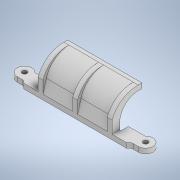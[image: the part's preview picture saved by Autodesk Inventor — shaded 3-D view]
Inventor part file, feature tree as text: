
AUTODESK INVENTOR PART (.ipt)
format: ipt  version: 2022 (Build 260153000, 153)  size: 208,384 bytes
history: native  units: mm
features: sketch x4, extrude x3, mirror x1, plane x1, pattern_linear x1
ambient origin geometry x8: Origin, YZ Plane, XZ Plane, XY Plane, X Axis, Y Axis, Z Axis, Center Point
bodies: Solid1 (feature_tree)
feature tree (10):
  extrude  "Extrusion1"  Depth=6.0mm
  extrude  "Extrusion2"  TaperAngle=0.0deg  [1 undecoded]
  mirror  "Mirror1"
  plane  "Work Plane1"
  extrude  "Extrusion3"  Depth=3.0mm
  pattern_linear  "Rectangular Pattern1"  Spacing1=4.0mm  [1 undecoded]
  sketch  "Sketch5"  dims[d7=4.0mm d8=4.0mm d9=4.0mm d10=2.0mm d11=2.0mm d12=0.0mm d13=2.0mm d14=9.0mm d15=10.0mm d16=12.0mm d17=3.0mm d20=15.0mm d21=2.5mm d22=7.5mm d23=12.0mm d24=2.0mm d25=15.0mm d26=0.0mm d27=2.0mm d28=0.0mm d29=20.0mm d31=14.0mm d32=20.0mm d34=14.0mm]
  sketch  "Sketch1"  dims[d0=24.5mm d1=6.0mm]
  sketch  "Sketch2"  dims[d2=2.0mm d3=0.0mm]
  sketch  "Sketch4"  dims[d4=0.0mm d6=3.0mm]
note: 2 required parameter values undecoded (feature->parameter linkage not recoverable at this tier; creation-order binding heuristic only, values carry confidence <= 0.55)
